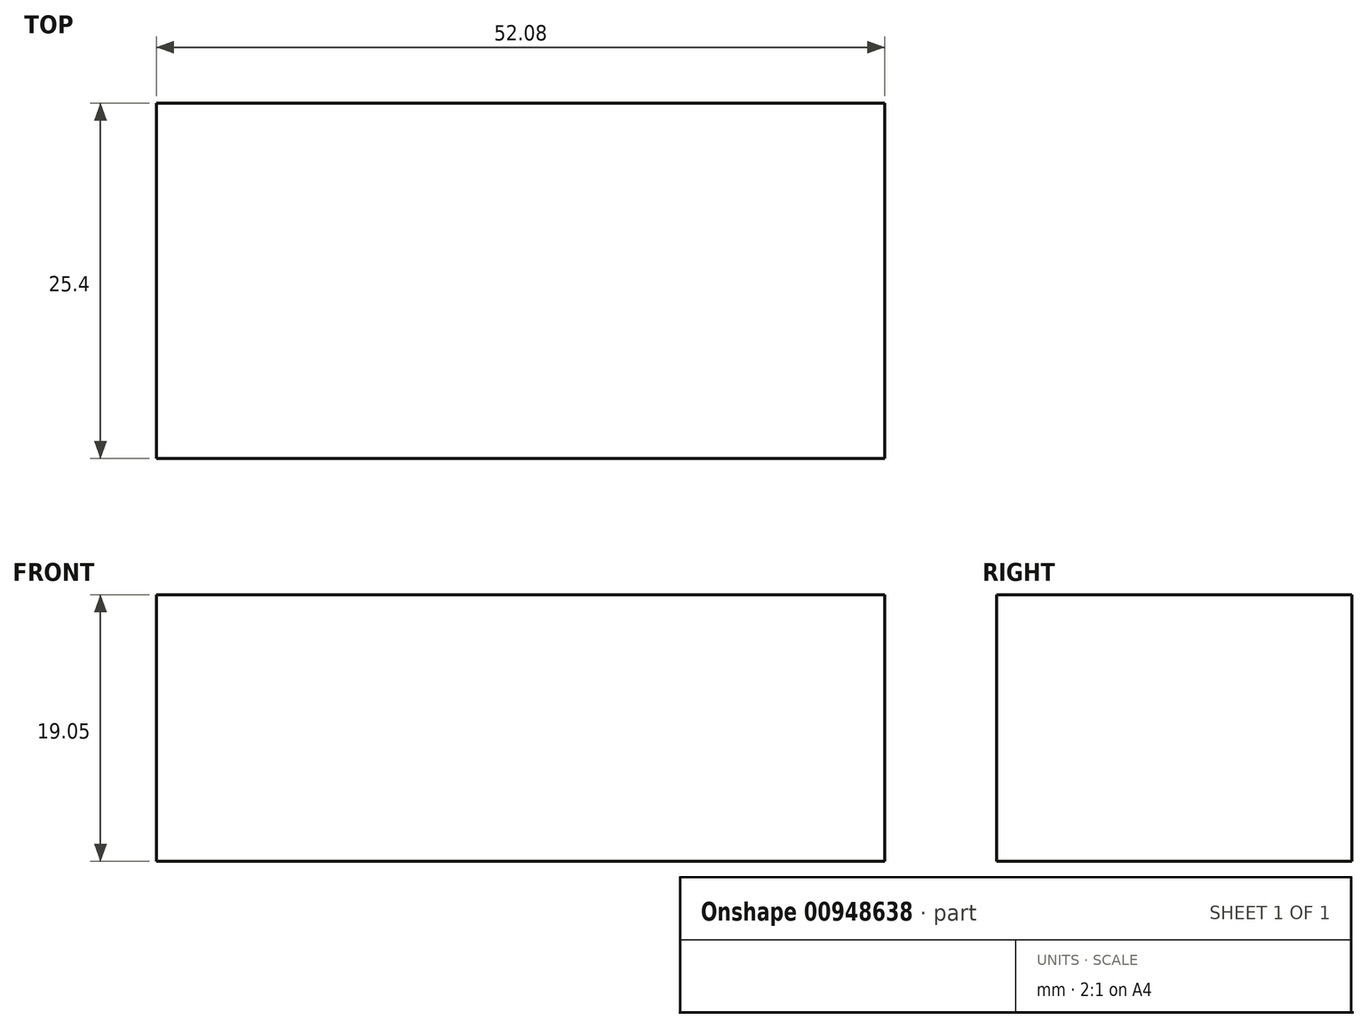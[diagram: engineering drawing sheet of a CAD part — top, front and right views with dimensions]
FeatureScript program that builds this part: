
annotation { "Feature Type Name" : "Feature", "Feature Type Description" : "" }
export const myFeature = defineFeature(function(context is Context, id is Id, definition is map)
    precondition{}
    {
        {
            var Q0;
            Q0=qCreatedBy(makeId("Top.planeOp"),FACE);
            var sketch = newSketch(context, id + "F0", { "sketchPlane" : qUnion([Q0])});
            skLineSegment(sketch, "E0.bottom", {"start": v(26.04, -12.7) * mm, "end": v(-26.04, -12.7) * mm});
            skLineSegment(sketch, "E0.top", {"start": v(26.04, 12.7) * mm, "end": v(-26.04, 12.7) * mm});
            skLineSegment(sketch, "E0.left", {"start": v(26.04, -12.7) * mm, "end": v(26.04, 12.7) * mm});
            skLineSegment(sketch, "E0.right", {"start": v(-26.04, -12.7) * mm, "end": v(-26.04, 12.7) * mm});
            skPoint(sketch, "E0.middle", {"position": v(0, 0) * mm});
            skSolve(sketch);
        }
        {
            var Q0;
            Q0=makeQuery(id+"F0.imprint","IMPRINT",FACE,{"disambiguationData":[TD([[makeQuery(id+"F0.imprint","IMPRINT",EDGE,{"derivedFrom":sQuery(id+"F0.wireOp",EDGE,"E0.bottom")}),-1.0]])]});
            extrude(context, id + "F1", {"entities" : qUnion([Q0]), "depth" : 19.05 * mm, "offsetDistance" : 25.4 * mm});
        }
    });
